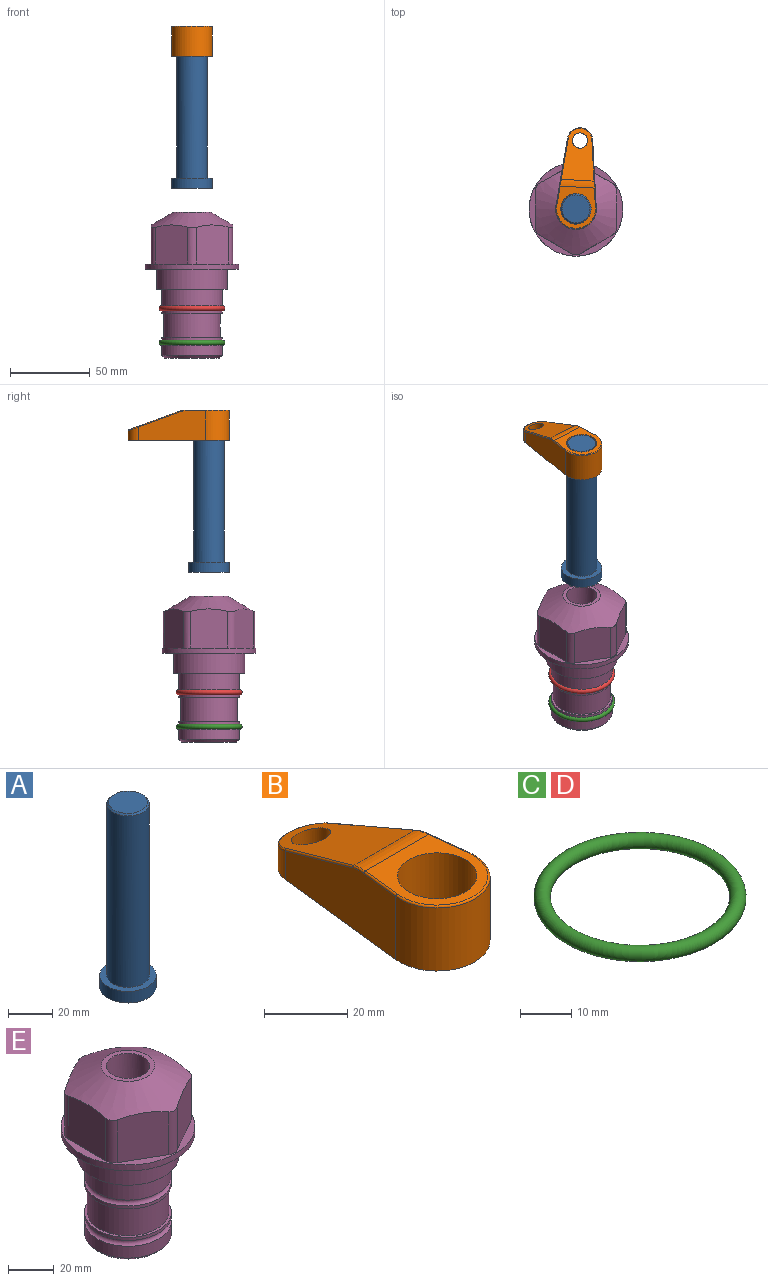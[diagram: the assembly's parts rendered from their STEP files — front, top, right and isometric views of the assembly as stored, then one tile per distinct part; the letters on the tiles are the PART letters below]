
ASSEMBLY  parts=5 mates=3
PART A: 6 faces, bbox 25.4x25.4x101.6 mm
  f0: plane 17.46x17.46mm, normal (0,0,1), area 239.5mm2, adj f5
  f1: plane 25.4x25.4mm, normal (0,0,-1), area 506.7mm2, adj f2
  f2: cylinder r=12.7mm len=25.4mm, axis (0,0,1), area 506.7mm2, adj f1,f3
  f3: plane 25.4x25.4mm, normal (0,0,1), area 221.7mm2, adj f2,f4
  f4: cylinder r=9.53mm len=94.46mm, axis (0,0,1), area 5653mm2, adj f3,f5
  f5: cone r=8.73mm half-angle=45deg, axis (0,0,-1), area 64.4mm2, adj f0,f4
PART B: 44 faces, bbox 27.5x64.5x19.1 mm
  f0: plane 2.3x0.95mm, normal (0,0,-1), area 1mm2, adj f25,f30,f34
  f1: plane 63.5x25.4mm, normal (0,0,-1), area 561.7mm2, adj f2,f3,f4,f5,f6,f7,f19,f20
  f2: cylinder r=12.7mm len=25.4mm, axis (0,0,-1), area 792.2mm2, adj f1,f3,f5,f13
  f3: plane 42.33x18.54mm, normal (0.99,0.11,0), area 647mm2, adj f1,f2,f4,f11,f12,f14
  f4: cylinder r=7.94mm len=15.78mm, axis (0,0,-1), area 158.6mm2, adj f1,f3,f5,f16
  f5: plane 42.33x18.54mm, normal (-0.99,0.11,0), area 647mm2, adj f1,f2,f4,f15,f17,f18
  f6: cylinder r=9.53mm len=19.05mm, axis (0,0,-1), area 1140.1mm2, adj f1,f8
  f7: cylinder r=4.76mm len=10.98mm, axis (0,0,-1), area 276.1mm2, adj f1,f9
  f8: plane 25.83x24.38mm, normal (0,0,1), area 262.2mm2, adj f6,f10,f11,f13,f15
  f9: plane 32.49x20.55mm, normal (0,0.34,0.94), area 489.9mm2, adj f7,f10,f14,f16,f18
  f10: cylinder r=12.7mm len=21.49mm, axis (-1,0,0), area 93.2mm2, adj f8,f9,f12,f17
  f11: cylinder r=0.51mm len=12.34mm, axis (0.11,-0.99,0), area 9.9mm2, adj f3,f8,f12,f13
  f12: bspline ~7.62x1.64mm, area 3.5mm2, adj f3,f10,f11,f14
  f13: torus R=12.19mm, axis (0,0,1), area 33.6mm2, adj f2,f8,f11,f15
  f14: cylinder r=0.51mm len=26.01mm, axis (0.1,-0.93,0.34), area 21.6mm2, adj f3,f9,f12,f16
  f15: cylinder r=0.51mm len=12.34mm, axis (0.11,0.99,0), area 9.9mm2, adj f5,f8,f13,f17
  f16: bspline ~15.78x7.05mm, area 15.7mm2, adj f4,f9,f14,f18
  f17: bspline ~7.62x1.64mm, area 3.5mm2, adj f5,f10,f15,f18
  f18: cylinder r=0.51mm len=26.01mm, axis (0.1,0.93,-0.34), area 21.6mm2, adj f5,f9,f16,f17
  f19: plane 21.6x14.29mm, normal (-0.99,-0.11,0), area 242.6mm2, adj f1,f26,f28,f34,f36,f38
  f20: plane 21.6x14.29mm, normal (0.99,-0.11,0), area 242.6mm2, adj f1,f27,f29,f37,f39,f41
  f21: cylinder r=12.7mm len=14.29mm, axis (0,0,-1), area 173.2mm2, adj f1,f26,f27,f30,f31,f33
  f22: cylinder r=7.94mm len=7.63mm, axis (0,0,-1), area 53.8mm2, adj f1,f28,f29,f42
  f23: plane 2.3x0.95mm, normal (0,0,-1), area 1mm2, adj f25,f33,f37
  f24: plane 17.94x12.32mm, normal (0,-0.34,-0.94), area 191.2mm2, adj f25,f38,f41,f42
  f25: cylinder r=9.53mm len=12.93mm, axis (-1,0,0), area 37.5mm2, adj f0,f23,f24,f31,f36,f39
  f26: cylinder r=1.59mm len=14.29mm, axis (0,0,-1), area 49mm2, adj f1,f19,f21,f32
  f27: cylinder r=1.59mm len=14.29mm, axis (0,0,-1), area 49mm2, adj f1,f20,f21,f35
  f28: cylinder r=1.59mm len=7.28mm, axis (0,0,-1), area 22.1mm2, adj f1,f19,f22,f40
  f29: cylinder r=1.59mm len=7.28mm, axis (0,0,-1), area 22.1mm2, adj f1,f20,f22,f43
  f30: torus R=14.29mm, axis (0,0,1), area 5.8mm2, adj f0,f21,f31,f32
  f31: bspline ~11.06x2.73mm, area 20.8mm2, adj f21,f25,f30,f33
  f32: sphere r=1.59mm, area 5.4mm2, adj f26,f30,f34
  f33: torus R=14.29mm, axis (0,0,1), area 5.8mm2, adj f21,f23,f31,f35
  f34: cylinder r=1.59mm len=1.68mm, axis (-0.11,0.99,0), area 2.4mm2, adj f0,f19,f32,f36
  f35: sphere r=1.59mm, area 5.4mm2, adj f27,f33,f37
  f36: bspline ~5.82x2.33mm, area 7.7mm2, adj f19,f25,f34,f38
  f37: cylinder r=1.59mm len=1.68mm, axis (0.11,0.99,0), area 2.4mm2, adj f20,f23,f35,f39
  f38: cylinder r=1.59mm len=18.33mm, axis (0.1,-0.93,0.34), area 46.7mm2, adj f19,f24,f36,f40
  f39: bspline ~5.82x2.33mm, area 7.7mm2, adj f20,f25,f37,f41
  f40: sphere r=1.59mm, area 3.6mm2, adj f28,f38,f42
  f41: cylinder r=1.59mm len=18.33mm, axis (0.1,0.93,-0.34), area 46.7mm2, adj f20,f24,f39,f43
  f42: bspline ~8.31x1.84mm, area 15.3mm2, adj f22,f24,f40,f43
  f43: sphere r=1.59mm, area 3.6mm2, adj f29,f41,f42
PART C: 1 faces, bbox 44.7x44.7x3.2 mm
  f0: torus R=19.05mm, axis (0,0,1), area 1193.9mm2
PART D: same geometry as C
PART E: 36 faces, bbox 58.7x58.7x91.2 mm
  f0: cylinder r=17.78mm len=35.56mm, axis (0,0,1), area 1670.8mm2, adj f23,f24,f31
  f1: cylinder r=19.05mm len=38.1mm, axis (0,0,1), area 1191.9mm2, adj f26,f27,f30
  f2: plane 58.66x58.66mm, normal (0,0,-1), area 1150.6mm2, adj f3,f28
  f3: cylinder r=29.33mm len=58.66mm, axis (0,0,-1), area 585.1mm2, adj f2,f4
  f4: plane 58.66x58.66mm, normal (0,0,1), area 475.9mm2, adj f3,f5,f6,f7,f8,f9,f10,f11
  f5: plane 24.5x20.32mm, normal (-0.5,0.87,0), area 562.8mm2, adj f4,f15,f16,f17
  f6: plane 24.5x20.32mm, normal (0.5,0.87,0), area 562.8mm2, adj f4,f14,f15,f17
  f7: plane 24.5x23.48mm, normal (1,0,0), area 562.8mm2, adj f4,f13,f14,f17
  f8: plane 24.5x20.32mm, normal (0.5,-0.87,0), area 562.8mm2, adj f4,f12,f13,f17
  f9: plane 24.5x20.32mm, normal (-0.5,-0.87,0), area 562.8mm2, adj f4,f11,f12,f17
  f10: plane 24.5x23.48mm, normal (-1,0,0), area 562.8mm2, adj f4,f11,f16,f17
  f11: cylinder r=5.08mm len=23.01mm, axis (0,0,-1), area 121.2mm2, adj f4,f9,f10,f17
  f12: cylinder r=5.08mm len=23.01mm, axis (0,0,-1), area 121.2mm2, adj f4,f8,f9,f17
  f13: cylinder r=5.08mm len=23.01mm, axis (0,0,-1), area 121.2mm2, adj f4,f7,f8,f17
  f14: cylinder r=5.08mm len=23.01mm, axis (0,0,-1), area 121.2mm2, adj f4,f6,f7,f17
  f15: cylinder r=5.08mm len=23.01mm, axis (0,0,-1), area 121.2mm2, adj f4,f5,f6,f17
  f16: cylinder r=5.08mm len=23.01mm, axis (0,0,-1), area 121.2mm2, adj f4,f5,f10,f17
  f17: cone r=11.73mm half-angle=60deg, axis (0,0,-1), area 2071.8mm2, adj f5,f6,f7,f8,f9,f10,f11,f12
  f18: plane 23.46x23.46mm, normal (0,0,1), area 147.4mm2, adj f17,f35
  f19: plane 34.93x34.93mm, normal (0,0,-1), area 958mm2, adj f29
  f20: cylinder r=19.05mm len=38.1mm, axis (0,0,1), area 760.1mm2, adj f21,f29
  f21: torus R=19.05mm, axis (0,0,1), area 565.3mm2, adj f20,f22
  f22: cylinder r=19.05mm len=38.1mm, axis (0,0,1), area 190mm2, adj f21,f23
  f23: plane 38.1x38.1mm, normal (0,0,1), area 146.9mm2, adj f0,f22
  f24: plane 38.1x38.1mm, normal (0,0,-1), area 146.9mm2, adj f0,f25
  f25: cylinder r=19.05mm len=38.1mm, axis (0,0,1), area 190mm2, adj f24,f26
  f26: torus R=19.05mm, axis (0,0,1), area 565.3mm2, adj f1,f25
  f27: plane 44.45x44.45mm, normal (0,0,-1), area 411.7mm2, adj f1,f28
  f28: cylinder r=22.23mm len=44.45mm, axis (0,0,1), area 1773.5mm2, adj f2,f27
  f29: cone r=19.05mm half-angle=45deg, axis (0,0,1), area 257.5mm2, adj f19,f20
  f30: cylinder r=3.17mm len=6.75mm, axis (-1,0,0), area 128mm2, adj f1,f33
  f31: cylinder r=3.17mm len=6.35mm, axis (-1,0,0), area 102.5mm2, adj f0,f33
  f32: plane 25.4x25.4mm, normal (0,0,1), area 506.7mm2, adj f33
  f33: cylinder r=12.7mm len=66.42mm, axis (0,0,-1), area 5236.2mm2, adj f30,f31,f32,f34
  f34: cone r=9.53mm half-angle=30deg, axis (0,0,-1), area 443.4mm2, adj f33,f35
  f35: cylinder r=9.53mm len=19.05mm, axis (0,0,-1), area 849mm2, adj f18,f34
PLACE A rot(axis=(0,0,1),86.7deg) t=(-0.24,-12.88,74.05)mm
PLACE B rot(axis=(0,0,-1),3.3deg) t=(-0.24,-12.88,128.66)mm
PLACE C t=(-0.24,-12.88,-26.03)mm
PLACE D t=(-0.24,-12.88,-4.44)mm
PLACE E t=(-0.24,-12.88,-4.44)mm
MATE fastened C.f0 <-> E.f0  axis (0,0,1) through (-0.24,-12.88,-50.54)mm
MATE cylindrical A.f2 <-> E.f0  axis (0,0,1) through (-0.24,-12.88,99.69)mm
MATE fastened B.f2 <-> A.f2  axis (0,0,1) through (-0.24,-12.88,147.71)mm
